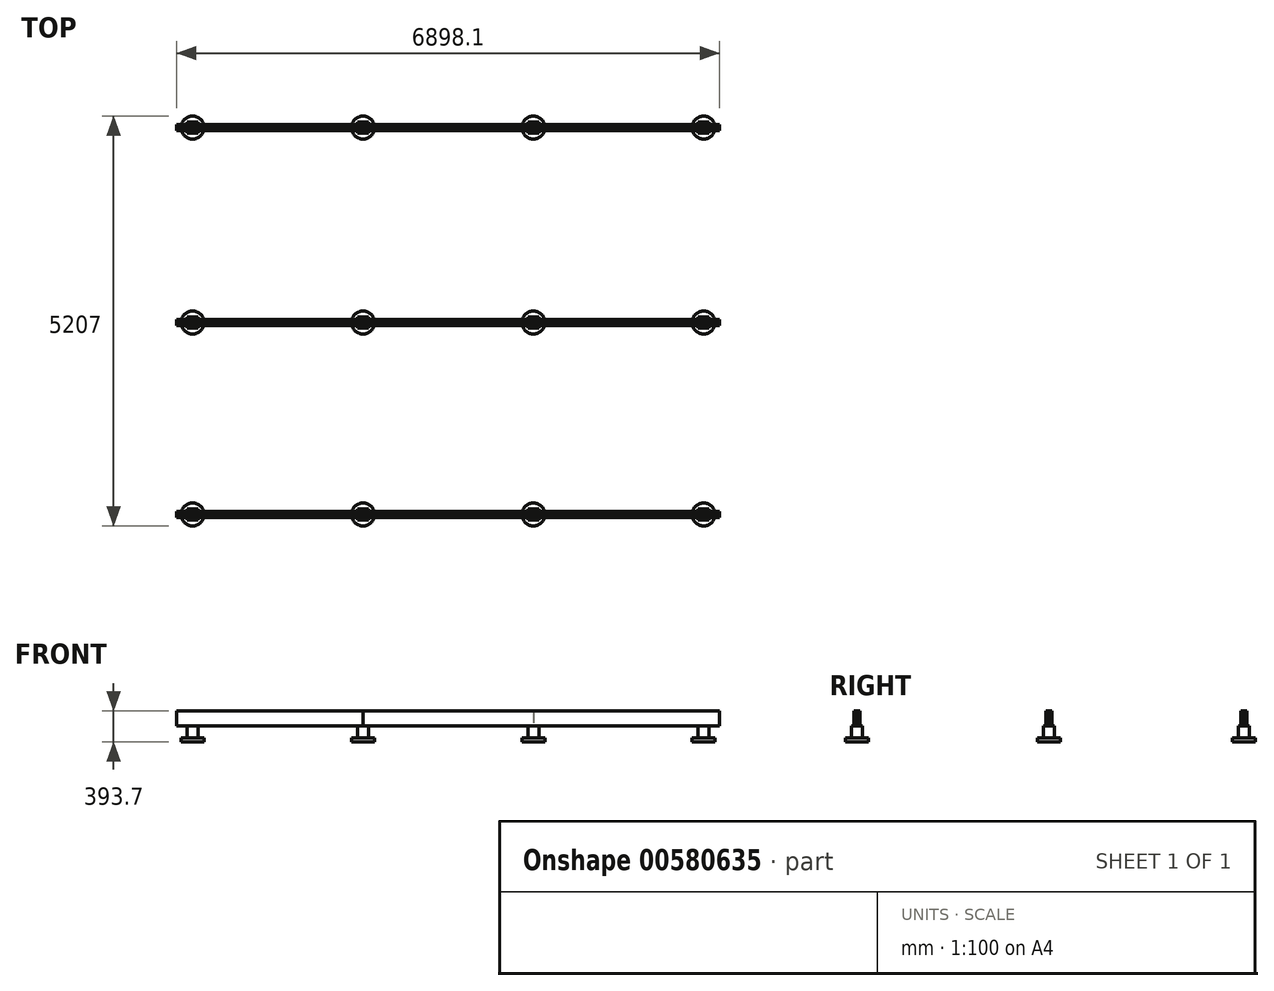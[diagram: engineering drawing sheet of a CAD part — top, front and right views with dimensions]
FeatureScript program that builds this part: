
annotation { "Feature Type Name" : "Feature", "Feature Type Description" : "" }
export const myFeature = defineFeature(function(context is Context, id is Id, definition is map)
    precondition{}
    {
        {
            var Q0;
            Q0=qCreatedBy(makeId("Top.planeOp"),FACE);
            var sketch = newSketch(context, id + "F0", { "sketchPlane" : qUnion([Q0])});
            skCircle(sketch, "E0", {"center": v(0, 0) * mm, "radius": 146.05 * mm});
            skCircle(sketch, "E1", {"center": v(2163.83, 0) * mm, "radius": 146.05 * mm});
            skCircle(sketch, "E2", {"center": v(4327.65, 0) * mm, "radius": 146.05 * mm});
            skCircle(sketch, "E3", {"center": v(6491.48, 0) * mm, "radius": 146.05 * mm});
            skCircle(sketch, "E4", {"center": v(0, -2476.5) * mm, "radius": 146.05 * mm});
            skCircle(sketch, "E5", {"center": v(2163.83, -2476.5) * mm, "radius": 146.05 * mm});
            skCircle(sketch, "E6", {"center": v(4327.65, -2476.5) * mm, "radius": 146.05 * mm});
            skCircle(sketch, "E7", {"center": v(6491.48, -2476.5) * mm, "radius": 146.05 * mm});
            skCircle(sketch, "E8", {"center": v(0, -4914.9) * mm, "radius": 146.05 * mm});
            skCircle(sketch, "E9", {"center": v(2163.83, -4914.9) * mm, "radius": 146.05 * mm});
            skCircle(sketch, "E10", {"center": v(4327.65, -4914.9) * mm, "radius": 146.05 * mm});
            skCircle(sketch, "E11", {"center": v(6491.48, -4914.9) * mm, "radius": 146.05 * mm});
            skSolve(sketch);
        }
        {
            var Q0;
            Q0=makeQuery(id+"F0.imprint","IMPRINT",FACE,{"disambiguationData":[TD([[makeQuery(id+"F0.imprint","IMPRINT",EDGE,{"derivedFrom":sQuery(id+"F0.wireOp",EDGE,"E3")}),1.0]])]});
            var Q1;
            Q1=makeQuery(id+"F0.imprint","IMPRINT",FACE,{"disambiguationData":[TD([[makeQuery(id+"F0.imprint","IMPRINT",EDGE,{"derivedFrom":sQuery(id+"F0.wireOp",EDGE,"E11")}),1.0]])]});
            var Q2;
            Q2=makeQuery(id+"F0.imprint","IMPRINT",FACE,{"disambiguationData":[TD([[makeQuery(id+"F0.imprint","IMPRINT",EDGE,{"derivedFrom":sQuery(id+"F0.wireOp",EDGE,"E5")}),1.0]])]});
            var Q3;
            Q3=makeQuery(id+"F0.imprint","IMPRINT",FACE,{"disambiguationData":[TD([[makeQuery(id+"F0.imprint","IMPRINT",EDGE,{"derivedFrom":sQuery(id+"F0.wireOp",EDGE,"E9")}),1.0]])]});
            var Q4;
            Q4=makeQuery(id+"F0.imprint","IMPRINT",FACE,{"disambiguationData":[TD([[makeQuery(id+"F0.imprint","IMPRINT",EDGE,{"derivedFrom":sQuery(id+"F0.wireOp",EDGE,"E4")}),1.0]])]});
            var Q5;
            Q5=makeQuery(id+"F0.imprint","IMPRINT",FACE,{"disambiguationData":[TD([[makeQuery(id+"F0.imprint","IMPRINT",EDGE,{"derivedFrom":sQuery(id+"F0.wireOp",EDGE,"E1")}),1.0]])]});
            var Q6;
            Q6=makeQuery(id+"F0.imprint","IMPRINT",FACE,{"disambiguationData":[TD([[makeQuery(id+"F0.imprint","IMPRINT",EDGE,{"derivedFrom":sQuery(id+"F0.wireOp",EDGE,"E10")}),1.0]])]});
            var Q7;
            Q7=makeQuery(id+"F0.imprint","IMPRINT",FACE,{"disambiguationData":[TD([[makeQuery(id+"F0.imprint","IMPRINT",EDGE,{"derivedFrom":sQuery(id+"F0.wireOp",EDGE,"E0")}),1.0]])]});
            var Q8;
            Q8=makeQuery(id+"F0.imprint","IMPRINT",FACE,{"disambiguationData":[TD([[makeQuery(id+"F0.imprint","IMPRINT",EDGE,{"derivedFrom":sQuery(id+"F0.wireOp",EDGE,"E2")}),1.0]])]});
            var Q9;
            Q9=makeQuery(id+"F0.imprint","IMPRINT",FACE,{"disambiguationData":[TD([[makeQuery(id+"F0.imprint","IMPRINT",EDGE,{"derivedFrom":sQuery(id+"F0.wireOp",EDGE,"E6")}),1.0]])]});
            var Q10;
            Q10=makeQuery(id+"F0.imprint","IMPRINT",FACE,{"disambiguationData":[TD([[makeQuery(id+"F0.imprint","IMPRINT",EDGE,{"derivedFrom":sQuery(id+"F0.wireOp",EDGE,"E7")}),1.0]])]});
            var Q11;
            Q11=makeQuery(id+"F0.imprint","IMPRINT",FACE,{"disambiguationData":[TD([[makeQuery(id+"F0.imprint","IMPRINT",EDGE,{"derivedFrom":sQuery(id+"F0.wireOp",EDGE,"E8")}),1.0]])]});
            extrude(context, id + "F1", {"entities" : qUnion([Q0, Q1, Q2, Q3, Q4, Q5, Q6, Q7, Q8, Q9, Q10, Q11]), "depth" : 50.8 * mm, "offsetDistance" : 25.4 * mm});
        }
        {
            var Q0;
            Q0=makeQuery(id+"F1.opExtrude","CAP_FACE",FACE,{"disambiguationData":[OSD([sQuery(id+"F0.wireOp",EDGE,"E0")])],"isStart":false});
            var sketch = newSketch(context, id + "F2", { "sketchPlane" : qUnion([Q0])});
            skLineSegment(sketch, "E12.bottom", {"start": v(69.85, -69.85) * mm, "end": v(-69.85, -69.85) * mm});
            skLineSegment(sketch, "E12.top", {"start": v(69.85, 69.85) * mm, "end": v(-69.85, 69.85) * mm});
            skLineSegment(sketch, "E12.left", {"start": v(69.85, -69.85) * mm, "end": v(69.85, 69.85) * mm});
            skLineSegment(sketch, "E12.right", {"start": v(-69.85, -69.85) * mm, "end": v(-69.85, 69.85) * mm});
            skPoint(sketch, "E12.middle", {"position": v(0, 0) * mm});
            skLineSegment(sketch, "E13.bottom", {"start": v(2233.68, -69.85) * mm, "end": v(2093.98, -69.85) * mm});
            skLineSegment(sketch, "E13.top", {"start": v(2233.68, 69.85) * mm, "end": v(2093.98, 69.85) * mm});
            skLineSegment(sketch, "E13.left", {"start": v(2233.68, -69.85) * mm, "end": v(2233.68, 69.85) * mm});
            skLineSegment(sketch, "E13.right", {"start": v(2093.98, -69.85) * mm, "end": v(2093.98, 69.85) * mm});
            skPoint(sketch, "E13.middle", {"position": v(2163.83, 0) * mm});
            skPoint(sketch, "E13.middle.positionSnap0", {"position": v(69.85, 0) * mm});
            skPoint(sketch, "E13.centerSnap0", {"position": v(69.85, 0) * mm});
            skLineSegment(sketch, "E14.bottom", {"start": v(4397.5, -69.85) * mm, "end": v(4257.8, -69.85) * mm});
            skLineSegment(sketch, "E14.top", {"start": v(4397.5, 69.85) * mm, "end": v(4257.8, 69.85) * mm});
            skLineSegment(sketch, "E14.left", {"start": v(4397.5, -69.85) * mm, "end": v(4397.5, 69.85) * mm});
            skLineSegment(sketch, "E14.right", {"start": v(4257.8, -69.85) * mm, "end": v(4257.8, 69.85) * mm});
            skPoint(sketch, "E14.middle", {"position": v(4327.65, 0) * mm});
            skLineSegment(sketch, "E15.bottom", {"start": v(6561.33, -69.85) * mm, "end": v(6421.63, -69.85) * mm});
            skLineSegment(sketch, "E15.top", {"start": v(6561.33, 69.85) * mm, "end": v(6421.63, 69.85) * mm});
            skLineSegment(sketch, "E15.left", {"start": v(6561.33, -69.85) * mm, "end": v(6561.33, 69.85) * mm});
            skLineSegment(sketch, "E15.right", {"start": v(6421.63, -69.85) * mm, "end": v(6421.63, 69.85) * mm});
            skPoint(sketch, "E15.middle", {"position": v(6491.48, 0) * mm});
            skLineSegment(sketch, "E16.bottom", {"start": v(69.85, -2546.35) * mm, "end": v(-69.85, -2546.35) * mm});
            skLineSegment(sketch, "E16.top", {"start": v(69.85, -2406.65) * mm, "end": v(-69.85, -2406.65) * mm});
            skLineSegment(sketch, "E16.left", {"start": v(69.85, -2546.35) * mm, "end": v(69.85, -2406.65) * mm});
            skLineSegment(sketch, "E16.right", {"start": v(-69.85, -2546.35) * mm, "end": v(-69.85, -2406.65) * mm});
            skPoint(sketch, "E16.middle", {"position": v(0, -2476.5) * mm});
            skLineSegment(sketch, "E17.bottom", {"start": v(2233.68, -2546.35) * mm, "end": v(2093.98, -2546.35) * mm});
            skLineSegment(sketch, "E17.top", {"start": v(2233.68, -2406.65) * mm, "end": v(2093.98, -2406.65) * mm});
            skLineSegment(sketch, "E17.left", {"start": v(2233.68, -2546.35) * mm, "end": v(2233.68, -2406.65) * mm});
            skLineSegment(sketch, "E17.right", {"start": v(2093.98, -2546.35) * mm, "end": v(2093.98, -2406.65) * mm});
            skPoint(sketch, "E17.middle", {"position": v(2163.83, -2476.5) * mm});
            skLineSegment(sketch, "E18.bottom", {"start": v(4397.5, -2546.35) * mm, "end": v(4257.8, -2546.35) * mm});
            skLineSegment(sketch, "E18.top", {"start": v(4397.5, -2406.65) * mm, "end": v(4257.8, -2406.65) * mm});
            skLineSegment(sketch, "E18.left", {"start": v(4397.5, -2546.35) * mm, "end": v(4397.5, -2406.65) * mm});
            skLineSegment(sketch, "E18.right", {"start": v(4257.8, -2546.35) * mm, "end": v(4257.8, -2406.65) * mm});
            skPoint(sketch, "E18.middle", {"position": v(4327.65, -2476.5) * mm});
            skLineSegment(sketch, "E19.bottom", {"start": v(6561.33, -2546.35) * mm, "end": v(6421.63, -2546.35) * mm});
            skLineSegment(sketch, "E19.top", {"start": v(6561.33, -2406.65) * mm, "end": v(6421.63, -2406.65) * mm});
            skLineSegment(sketch, "E19.left", {"start": v(6561.33, -2546.35) * mm, "end": v(6561.33, -2406.65) * mm});
            skLineSegment(sketch, "E19.right", {"start": v(6421.63, -2546.35) * mm, "end": v(6421.63, -2406.65) * mm});
            skPoint(sketch, "E19.middle", {"position": v(6491.48, -2476.5) * mm});
            skLineSegment(sketch, "E20.bottom", {"start": v(69.85, -4984.75) * mm, "end": v(-69.85, -4984.75) * mm});
            skLineSegment(sketch, "E20.top", {"start": v(69.85, -4845.05) * mm, "end": v(-69.85, -4845.05) * mm});
            skLineSegment(sketch, "E20.left", {"start": v(69.85, -4984.75) * mm, "end": v(69.85, -4845.05) * mm});
            skLineSegment(sketch, "E20.right", {"start": v(-69.85, -4984.75) * mm, "end": v(-69.85, -4845.05) * mm});
            skPoint(sketch, "E20.middle", {"position": v(0, -4914.9) * mm});
            skLineSegment(sketch, "E21.bottom", {"start": v(2233.68, -4984.75) * mm, "end": v(2093.98, -4984.75) * mm});
            skLineSegment(sketch, "E21.top", {"start": v(2233.68, -4845.05) * mm, "end": v(2093.98, -4845.05) * mm});
            skLineSegment(sketch, "E21.left", {"start": v(2233.68, -4984.75) * mm, "end": v(2233.68, -4845.05) * mm});
            skLineSegment(sketch, "E21.right", {"start": v(2093.98, -4984.75) * mm, "end": v(2093.98, -4845.05) * mm});
            skPoint(sketch, "E21.middle", {"position": v(2163.83, -4914.9) * mm});
            skLineSegment(sketch, "E22.bottom", {"start": v(4397.5, -4984.75) * mm, "end": v(4257.8, -4984.75) * mm});
            skLineSegment(sketch, "E22.top", {"start": v(4397.5, -4845.05) * mm, "end": v(4257.8, -4845.05) * mm});
            skLineSegment(sketch, "E22.left", {"start": v(4397.5, -4984.75) * mm, "end": v(4397.5, -4845.05) * mm});
            skLineSegment(sketch, "E22.right", {"start": v(4257.8, -4984.75) * mm, "end": v(4257.8, -4845.05) * mm});
            skPoint(sketch, "E22.middle", {"position": v(4327.65, -4914.9) * mm});
            skLineSegment(sketch, "E23.bottom", {"start": v(6561.33, -4984.75) * mm, "end": v(6421.63, -4984.75) * mm});
            skLineSegment(sketch, "E23.top", {"start": v(6561.33, -4845.05) * mm, "end": v(6421.63, -4845.05) * mm});
            skLineSegment(sketch, "E23.left", {"start": v(6561.33, -4984.75) * mm, "end": v(6561.33, -4845.05) * mm});
            skLineSegment(sketch, "E23.right", {"start": v(6421.63, -4984.75) * mm, "end": v(6421.63, -4845.05) * mm});
            skPoint(sketch, "E23.middle", {"position": v(6491.48, -4914.9) * mm});
            skSolve(sketch);
        }
        {
            var Q0;
            Q0 = qSketchRegion(id + "F2", true);
            extrude(context, id + "F3", {"entities" : qUnion([Q0]), "depth" : 152.4 * mm, "offsetDistance" : 25.4 * mm});
        }
        {
            var Q0;
            Q0=makeQuery(id+"F3.opExtrude","CAP_FACE",FACE,{"disambiguationData":[OSD([sQuery(id+"F2.wireOp",EDGE,"E12.bottom"),sQuery(id+"F2.wireOp",EDGE,"E12.top"),sQuery(id+"F2.wireOp",EDGE,"E12.left"),sQuery(id+"F2.wireOp",EDGE,"E12.right")])],"isStart":false});
            var sketch = newSketch(context, id + "F4", { "sketchPlane" : qUnion([Q0])});
            skLineSegment(sketch, "E24.bottom", {"start": v(2163.83, -38.1) * mm, "end": v(-203.2, -38.1) * mm});
            skLineSegment(sketch, "E24.top", {"start": v(2163.83, 0) * mm, "end": v(-203.2, 0) * mm});
            skLineSegment(sketch, "E24.left", {"start": v(2163.83, -38.1) * mm, "end": v(2163.83, 0) * mm});
            skLineSegment(sketch, "E24.right", {"start": v(-203.2, -38.1) * mm, "end": v(-203.2, 0) * mm});
            skPoint(sketch, "E24.middle", {"position": v(980.31, -19.05) * mm});
            skSolve(sketch);
        }
        {
            var Q0;
            Q0 = qSketchRegion(id + "F4", true);
            extrude(context, id + "F5", {"entities" : qUnion([Q0]), "depth" : 190.5 * mm, "offsetDistance" : 25.4 * mm});
        }
        {
            var Q0;
            Q0=makeQuery(id+"F3.opExtrude","CAP_FACE",FACE,{"disambiguationData":[OSD([sQuery(id+"F2.wireOp",EDGE,"E12.bottom"),sQuery(id+"F2.wireOp",EDGE,"E12.top"),sQuery(id+"F2.wireOp",EDGE,"E12.left"),sQuery(id+"F2.wireOp",EDGE,"E12.right")])],"isStart":false});
            var sketch = newSketch(context, id + "F6", { "sketchPlane" : qUnion([Q0])});
            skLineSegment(sketch, "E25.bottom", {"start": v(-203.2, 0) * mm, "end": v(4327.65, 0) * mm});
            skLineSegment(sketch, "E25.top", {"start": v(-203.2, 38.1) * mm, "end": v(4327.65, 38.1) * mm});
            skLineSegment(sketch, "E25.left", {"start": v(-203.2, 0) * mm, "end": v(-203.2, 38.1) * mm});
            skLineSegment(sketch, "E25.right", {"start": v(4327.65, 0) * mm, "end": v(4327.65, 38.1) * mm});
            skSolve(sketch);
        }
        {
            var Q0;
            {var subQ0=sQuery(id+"F6.wireOp",EDGE,"E25.right");Q0=makeQuery(id+"F6.imprint","IMPRINT",FACE,{"disambiguationData":[TD([[makeQuery(id+"F6.imprint","IMPRINT",EDGE,{"derivedFrom":subQ0}),1.0]])]});}
            var Q1;
            {var subQ0=sQuery(id+"F6.wireOp",EDGE,"E25.bottom");var subQ1=makeQuery(id+"F3.opExtrude","CAP_EDGE",EDGE,{"disambiguationData":[OSD([sQuery(id+"F2.wireOp",EDGE,"E12.right")])],"isStart":false});var subQ2=makeQuery(id+"F6.imprint","INTERSECT",VERTEX,{"derivedFrom":[subQ1,subQ0]});Q1=makeQuery(id+"F6.imprint","IMPRINT",FACE,{"disambiguationData":[TD([[makeQuery(id+"F6.imprint","IMPRINT",EDGE,{"disambiguationData":[TD([[subQ2,-1.0]])],"derivedFrom":subQ0}),1.0]])]});}
            var Q2;
            {var subQ0=sQuery(id+"F6.wireOp",EDGE,"E25.left");Q2=makeQuery(id+"F6.imprint","IMPRINT",FACE,{"disambiguationData":[TD([[makeQuery(id+"F6.imprint","IMPRINT",EDGE,{"derivedFrom":subQ0}),-1.0]])]});}
            extrude(context, id + "F7", {"entities" : qUnion([Q0, Q1, Q2]), "depth" : 190.5 * mm, "offsetDistance" : 25.4 * mm});
        }
        {
            var Q0;
            Q0=makeQuery(id+"F3.opExtrude","CAP_FACE",FACE,{"disambiguationData":[OSD([sQuery(id+"F2.wireOp",EDGE,"E16.bottom"),sQuery(id+"F2.wireOp",EDGE,"E16.top"),sQuery(id+"F2.wireOp",EDGE,"E16.left"),sQuery(id+"F2.wireOp",EDGE,"E16.right")])],"isStart":false});
            var sketch = newSketch(context, id + "F8", { "sketchPlane" : qUnion([Q0])});
            skLineSegment(sketch, "E26.bottom", {"start": v(-203.2, -2438.4) * mm, "end": v(4327.87, -2438.4) * mm});
            skLineSegment(sketch, "E26.top", {"start": v(-203.2, -2476.5) * mm, "end": v(4327.87, -2476.5) * mm});
            skLineSegment(sketch, "E26.left", {"start": v(-203.2, -2438.4) * mm, "end": v(-203.2, -2476.5) * mm});
            skLineSegment(sketch, "E26.right", {"start": v(4327.87, -2438.4) * mm, "end": v(4327.87, -2476.5) * mm});
            skSolve(sketch);
        }
        {
            var Q0;
            {var subQ0=sQuery(id+"F8.wireOp",EDGE,"E26.bottom");var subQ1=makeQuery(id+"F3.opExtrude","CAP_EDGE",EDGE,{"disambiguationData":[OSD([sQuery(id+"F2.wireOp",EDGE,"E16.right")])],"isStart":false});var subQ2=makeQuery(id+"F8.imprint","INTERSECT",VERTEX,{"derivedFrom":[subQ1,subQ0]});Q0=makeQuery(id+"F8.imprint","IMPRINT",FACE,{"disambiguationData":[TD([[makeQuery(id+"F8.imprint","IMPRINT",EDGE,{"disambiguationData":[TD([[subQ2,-1.0]])],"derivedFrom":subQ0}),-1.0]])]});}
            var Q1;
            {var subQ0=sQuery(id+"F8.wireOp",EDGE,"E26.left");Q1=makeQuery(id+"F8.imprint","IMPRINT",FACE,{"disambiguationData":[TD([[makeQuery(id+"F8.imprint","IMPRINT",EDGE,{"derivedFrom":subQ0}),1.0]])]});}
            var Q2;
            {var subQ0=sQuery(id+"F8.wireOp",EDGE,"E26.right");Q2=makeQuery(id+"F8.imprint","IMPRINT",FACE,{"disambiguationData":[TD([[makeQuery(id+"F8.imprint","IMPRINT",EDGE,{"derivedFrom":subQ0}),-1.0]])]});}
            extrude(context, id + "F9", {"entities" : qUnion([Q0, Q1, Q2]), "depth" : 190.5 * mm, "offsetDistance" : 25.4 * mm});
        }
        {
            var Q0;
            Q0=makeQuery(id+"F3.opExtrude","CAP_FACE",FACE,{"disambiguationData":[OSD([sQuery(id+"F2.wireOp",EDGE,"E14.bottom"),sQuery(id+"F2.wireOp",EDGE,"E14.top"),sQuery(id+"F2.wireOp",EDGE,"E14.left"),sQuery(id+"F2.wireOp",EDGE,"E14.right")])],"isStart":false});
            var sketch = newSketch(context, id + "F10", { "sketchPlane" : qUnion([Q0])});
            skLineSegment(sketch, "E27.bottom", {"start": v(4327.65, 38.1) * mm, "end": v(6694.68, 38.1) * mm});
            skLineSegment(sketch, "E27.top", {"start": v(4327.65, 0) * mm, "end": v(6694.68, 0) * mm});
            skLineSegment(sketch, "E27.left", {"start": v(4327.65, 38.1) * mm, "end": v(4327.65, 0) * mm});
            skLineSegment(sketch, "E27.right", {"start": v(6694.68, 38.1) * mm, "end": v(6694.68, 0) * mm});
            skSolve(sketch);
        }
        {
            var Q0;
            {var subQ0=sQuery(id+"F10.wireOp",EDGE,"E27.left");Q0=makeQuery(id+"F10.imprint","IMPRINT",FACE,{"disambiguationData":[TD([[makeQuery(id+"F10.imprint","IMPRINT",EDGE,{"derivedFrom":subQ0}),1.0]])]});}
            var Q1;
            {var subQ0=sQuery(id+"F10.wireOp",EDGE,"E27.right");Q1=makeQuery(id+"F10.imprint","IMPRINT",FACE,{"disambiguationData":[TD([[makeQuery(id+"F10.imprint","IMPRINT",EDGE,{"derivedFrom":subQ0}),-1.0]])]});}
            extrude(context, id + "F11", {"entities" : qUnion([Q0, Q1]), "depth" : 190.5 * mm, "offsetDistance" : 25.4 * mm});
        }
        {
            var Q0;
            Q0=makeQuery(id+"F3.opExtrude","CAP_FACE",FACE,{"disambiguationData":[OSD([sQuery(id+"F2.wireOp",EDGE,"E13.bottom"),sQuery(id+"F2.wireOp",EDGE,"E13.top"),sQuery(id+"F2.wireOp",EDGE,"E13.left"),sQuery(id+"F2.wireOp",EDGE,"E13.right")])],"isStart":false});
            var sketch = newSketch(context, id + "F12", { "sketchPlane" : qUnion([Q0])});
            skLineSegment(sketch, "E28.bottom", {"start": v(2163.83, 0) * mm, "end": v(6694.9, 0) * mm});
            skLineSegment(sketch, "E28.top", {"start": v(2163.83, -38.1) * mm, "end": v(6694.9, -38.1) * mm});
            skLineSegment(sketch, "E28.left", {"start": v(2163.83, 0) * mm, "end": v(2163.83, -38.1) * mm});
            skLineSegment(sketch, "E28.right", {"start": v(6694.9, 0) * mm, "end": v(6694.9, -38.1) * mm});
            skSolve(sketch);
        }
        {
            var Q0;
            {var subQ0=sQuery(id+"F12.wireOp",EDGE,"E28.left");Q0=makeQuery(id+"F12.imprint","IMPRINT",FACE,{"disambiguationData":[TD([[makeQuery(id+"F12.imprint","IMPRINT",EDGE,{"derivedFrom":subQ0}),1.0]])]});}
            var Q1;
            {var subQ0=sQuery(id+"F12.wireOp",EDGE,"E28.right");Q1=makeQuery(id+"F12.imprint","IMPRINT",FACE,{"disambiguationData":[TD([[makeQuery(id+"F12.imprint","IMPRINT",EDGE,{"derivedFrom":subQ0}),-1.0]])]});}
            extrude(context, id + "F13", {"entities" : qUnion([Q0, Q1]), "depth" : 190.5 * mm, "offsetDistance" : 25.4 * mm});
        }
        {
            var Q0;
            Q0=makeQuery(id+"F3.opExtrude","CAP_FACE",FACE,{"disambiguationData":[OSD([sQuery(id+"F2.wireOp",EDGE,"E20.bottom"),sQuery(id+"F2.wireOp",EDGE,"E20.top"),sQuery(id+"F2.wireOp",EDGE,"E20.left"),sQuery(id+"F2.wireOp",EDGE,"E20.right")])],"isStart":false});
            var sketch = newSketch(context, id + "F14", { "sketchPlane" : qUnion([Q0])});
            skLineSegment(sketch, "E29.bottom", {"start": v(-203.2, -4876.8) * mm, "end": v(4327.87, -4876.8) * mm});
            skLineSegment(sketch, "E29.top", {"start": v(-203.2, -4914.9) * mm, "end": v(4327.87, -4914.9) * mm});
            skLineSegment(sketch, "E29.left", {"start": v(-203.2, -4876.8) * mm, "end": v(-203.2, -4914.9) * mm});
            skLineSegment(sketch, "E29.right", {"start": v(4327.87, -4876.8) * mm, "end": v(4327.87, -4914.9) * mm});
            skSolve(sketch);
        }
        {
            var Q0;
            {var subQ0=sQuery(id+"F14.wireOp",EDGE,"E29.left");Q0=makeQuery(id+"F14.imprint","IMPRINT",FACE,{"disambiguationData":[TD([[makeQuery(id+"F14.imprint","IMPRINT",EDGE,{"derivedFrom":subQ0}),1.0]])]});}
            var Q1;
            {var subQ0=sQuery(id+"F14.wireOp",EDGE,"E29.bottom");var subQ1=makeQuery(id+"F3.opExtrude","CAP_EDGE",EDGE,{"disambiguationData":[OSD([sQuery(id+"F2.wireOp",EDGE,"E20.right")])],"isStart":false});var subQ2=makeQuery(id+"F14.imprint","INTERSECT",VERTEX,{"derivedFrom":[subQ1,subQ0]});Q1=makeQuery(id+"F14.imprint","IMPRINT",FACE,{"disambiguationData":[TD([[makeQuery(id+"F14.imprint","IMPRINT",EDGE,{"disambiguationData":[TD([[subQ2,-1.0]])],"derivedFrom":subQ0}),-1.0]])]});}
            var Q2;
            {var subQ0=sQuery(id+"F14.wireOp",EDGE,"E29.right");Q2=makeQuery(id+"F14.imprint","IMPRINT",FACE,{"disambiguationData":[TD([[makeQuery(id+"F14.imprint","IMPRINT",EDGE,{"derivedFrom":subQ0}),-1.0]])]});}
            extrude(context, id + "F15", {"entities" : qUnion([Q0, Q1, Q2]), "depth" : 190.5 * mm, "offsetDistance" : 25.4 * mm});
        }
        {
            var Q0;
            Q0=makeQuery(id+"F3.opExtrude","CAP_FACE",FACE,{"disambiguationData":[OSD([sQuery(id+"F2.wireOp",EDGE,"E16.bottom"),sQuery(id+"F2.wireOp",EDGE,"E16.top"),sQuery(id+"F2.wireOp",EDGE,"E16.left"),sQuery(id+"F2.wireOp",EDGE,"E16.right")])],"isStart":false});
            var sketch = newSketch(context, id + "F16", { "sketchPlane" : qUnion([Q0])});
            skLineSegment(sketch, "E30.bottom", {"start": v(-203.2, -2476.5) * mm, "end": v(2163.83, -2476.5) * mm});
            skLineSegment(sketch, "E30.top", {"start": v(-203.2, -2514.6) * mm, "end": v(2163.83, -2514.6) * mm});
            skLineSegment(sketch, "E30.left", {"start": v(-203.2, -2476.5) * mm, "end": v(-203.2, -2514.6) * mm});
            skLineSegment(sketch, "E30.right", {"start": v(2163.83, -2476.5) * mm, "end": v(2163.83, -2514.6) * mm});
            skSolve(sketch);
        }
        {
            var Q0;
            {var subQ0=sQuery(id+"F16.wireOp",EDGE,"E30.left");Q0=makeQuery(id+"F16.imprint","IMPRINT",FACE,{"disambiguationData":[TD([[makeQuery(id+"F16.imprint","IMPRINT",EDGE,{"derivedFrom":subQ0}),1.0]])]});}
            var Q1;
            {var subQ0=sQuery(id+"F16.wireOp",EDGE,"E30.bottom");var subQ1=makeQuery(id+"F3.opExtrude","CAP_EDGE",EDGE,{"disambiguationData":[OSD([sQuery(id+"F2.wireOp",EDGE,"E16.right")])],"isStart":false});var subQ2=makeQuery(id+"F16.imprint","INTERSECT",VERTEX,{"derivedFrom":[subQ1,subQ0]});Q1=makeQuery(id+"F16.imprint","IMPRINT",FACE,{"disambiguationData":[TD([[makeQuery(id+"F16.imprint","IMPRINT",EDGE,{"disambiguationData":[TD([[subQ2,-1.0]])],"derivedFrom":subQ0}),-1.0]])]});}
            var Q2;
            {var subQ0=sQuery(id+"F16.wireOp",EDGE,"E30.right");Q2=makeQuery(id+"F16.imprint","IMPRINT",FACE,{"disambiguationData":[TD([[makeQuery(id+"F16.imprint","IMPRINT",EDGE,{"derivedFrom":subQ0}),-1.0]])]});}
            extrude(context, id + "F17", {"entities" : qUnion([Q0, Q1, Q2]), "depth" : 190.5 * mm, "offsetDistance" : 25.4 * mm});
        }
        {
            var Q0;
            Q0=makeQuery(id+"F3.opExtrude","CAP_FACE",FACE,{"disambiguationData":[OSD([sQuery(id+"F2.wireOp",EDGE,"E20.bottom"),sQuery(id+"F2.wireOp",EDGE,"E20.top"),sQuery(id+"F2.wireOp",EDGE,"E20.left"),sQuery(id+"F2.wireOp",EDGE,"E20.right")])],"isStart":false});
            var sketch = newSketch(context, id + "F18", { "sketchPlane" : qUnion([Q0])});
            skLineSegment(sketch, "E31.bottom", {"start": v(-203.2, -4914.9) * mm, "end": v(2163.83, -4914.9) * mm});
            skLineSegment(sketch, "E31.top", {"start": v(-203.2, -4953) * mm, "end": v(2163.83, -4953) * mm});
            skLineSegment(sketch, "E31.left", {"start": v(-203.2, -4914.9) * mm, "end": v(-203.2, -4953) * mm});
            skLineSegment(sketch, "E31.right", {"start": v(2163.83, -4914.9) * mm, "end": v(2163.83, -4953) * mm});
            skSolve(sketch);
        }
        {
            var Q0;
            {var subQ0=sQuery(id+"F18.wireOp",EDGE,"E31.left");Q0=makeQuery(id+"F18.imprint","IMPRINT",FACE,{"disambiguationData":[TD([[makeQuery(id+"F18.imprint","IMPRINT",EDGE,{"derivedFrom":subQ0}),1.0]])]});}
            var Q1;
            {var subQ0=sQuery(id+"F18.wireOp",EDGE,"E31.bottom");var subQ1=makeQuery(id+"F3.opExtrude","CAP_EDGE",EDGE,{"disambiguationData":[OSD([sQuery(id+"F2.wireOp",EDGE,"E20.right")])],"isStart":false});var subQ2=makeQuery(id+"F18.imprint","INTERSECT",VERTEX,{"derivedFrom":[subQ1,subQ0]});Q1=makeQuery(id+"F18.imprint","IMPRINT",FACE,{"disambiguationData":[TD([[makeQuery(id+"F18.imprint","IMPRINT",EDGE,{"disambiguationData":[TD([[subQ2,-1.0]])],"derivedFrom":subQ0}),-1.0]])]});}
            var Q2;
            {var subQ0=sQuery(id+"F18.wireOp",EDGE,"E31.right");Q2=makeQuery(id+"F18.imprint","IMPRINT",FACE,{"disambiguationData":[TD([[makeQuery(id+"F18.imprint","IMPRINT",EDGE,{"derivedFrom":subQ0}),-1.0]])]});}
            extrude(context, id + "F19", {"entities" : qUnion([Q0, Q1, Q2]), "depth" : 190.5 * mm, "offsetDistance" : 25.4 * mm});
        }
        {
            var Q0;
            Q0=makeQuery(id+"F3.opExtrude","CAP_FACE",FACE,{"disambiguationData":[OSD([sQuery(id+"F2.wireOp",EDGE,"E17.bottom"),sQuery(id+"F2.wireOp",EDGE,"E17.top"),sQuery(id+"F2.wireOp",EDGE,"E17.left"),sQuery(id+"F2.wireOp",EDGE,"E17.right")])],"isStart":false});
            var sketch = newSketch(context, id + "F20", { "sketchPlane" : qUnion([Q0])});
            skLineSegment(sketch, "E32.bottom", {"start": v(2163.83, -2476.5) * mm, "end": v(6694.9, -2476.5) * mm});
            skLineSegment(sketch, "E32.top", {"start": v(2163.83, -2514.6) * mm, "end": v(6694.9, -2514.6) * mm});
            skLineSegment(sketch, "E32.left", {"start": v(2163.83, -2476.5) * mm, "end": v(2163.83, -2514.6) * mm});
            skLineSegment(sketch, "E32.right", {"start": v(6694.9, -2476.5) * mm, "end": v(6694.9, -2514.6) * mm});
            skSolve(sketch);
        }
        {
            var Q0;
            {var subQ0=sQuery(id+"F20.wireOp",EDGE,"E32.left");Q0=makeQuery(id+"F20.imprint","IMPRINT",FACE,{"disambiguationData":[TD([[makeQuery(id+"F20.imprint","IMPRINT",EDGE,{"derivedFrom":subQ0}),1.0]])]});}
            var Q1;
            {var subQ0=sQuery(id+"F20.wireOp",EDGE,"E32.right");Q1=makeQuery(id+"F20.imprint","IMPRINT",FACE,{"disambiguationData":[TD([[makeQuery(id+"F20.imprint","IMPRINT",EDGE,{"derivedFrom":subQ0}),-1.0]])]});}
            extrude(context, id + "F21", {"entities" : qUnion([Q0, Q1]), "depth" : 190.5 * mm, "offsetDistance" : 25.4 * mm});
        }
        {
            var Q0;
            Q0=makeQuery(id+"F3.opExtrude","CAP_FACE",FACE,{"disambiguationData":[OSD([sQuery(id+"F2.wireOp",EDGE,"E21.bottom"),sQuery(id+"F2.wireOp",EDGE,"E21.top"),sQuery(id+"F2.wireOp",EDGE,"E21.left"),sQuery(id+"F2.wireOp",EDGE,"E21.right")])],"isStart":false});
            var sketch = newSketch(context, id + "F22", { "sketchPlane" : qUnion([Q0])});
            skLineSegment(sketch, "E33.bottom", {"start": v(2163.83, -4914.9) * mm, "end": v(6694.9, -4914.9) * mm});
            skLineSegment(sketch, "E33.top", {"start": v(2163.83, -4953) * mm, "end": v(6694.9, -4953) * mm});
            skLineSegment(sketch, "E33.left", {"start": v(2163.83, -4914.9) * mm, "end": v(2163.83, -4953) * mm});
            skLineSegment(sketch, "E33.right", {"start": v(6694.9, -4914.9) * mm, "end": v(6694.9, -4953) * mm});
            skSolve(sketch);
        }
        {
            var Q0;
            {var subQ0=sQuery(id+"F22.wireOp",EDGE,"E33.right");Q0=makeQuery(id+"F22.imprint","IMPRINT",FACE,{"disambiguationData":[TD([[makeQuery(id+"F22.imprint","IMPRINT",EDGE,{"derivedFrom":subQ0}),-1.0]])]});}
            var Q1;
            {var subQ0=sQuery(id+"F22.wireOp",EDGE,"E33.left");Q1=makeQuery(id+"F22.imprint","IMPRINT",FACE,{"disambiguationData":[TD([[makeQuery(id+"F22.imprint","IMPRINT",EDGE,{"derivedFrom":subQ0}),1.0]])]});}
            extrude(context, id + "F23", {"entities" : qUnion([Q0, Q1]), "depth" : 190.5 * mm, "offsetDistance" : 25.4 * mm});
        }
        {
            var Q0;
            Q0=makeQuery(id+"F3.opExtrude","CAP_FACE",FACE,{"disambiguationData":[OSD([sQuery(id+"F2.wireOp",EDGE,"E18.bottom"),sQuery(id+"F2.wireOp",EDGE,"E18.top"),sQuery(id+"F2.wireOp",EDGE,"E18.left"),sQuery(id+"F2.wireOp",EDGE,"E18.right")])],"isStart":false});
            var sketch = newSketch(context, id + "F24", { "sketchPlane" : qUnion([Q0])});
            skLineSegment(sketch, "E34.bottom", {"start": v(4327.87, -2476.5) * mm, "end": v(6694.9, -2476.5) * mm});
            skLineSegment(sketch, "E34.top", {"start": v(4327.87, -2438.4) * mm, "end": v(6694.9, -2438.4) * mm});
            skLineSegment(sketch, "E34.left", {"start": v(4327.87, -2476.5) * mm, "end": v(4327.87, -2438.4) * mm});
            skLineSegment(sketch, "E34.right", {"start": v(6694.9, -2476.5) * mm, "end": v(6694.9, -2438.4) * mm});
            skSolve(sketch);
        }
        {
            var Q0;
            {var subQ0=sQuery(id+"F24.wireOp",EDGE,"E34.right");Q0=makeQuery(id+"F24.imprint","IMPRINT",FACE,{"disambiguationData":[TD([[makeQuery(id+"F24.imprint","IMPRINT",EDGE,{"derivedFrom":subQ0}),1.0]])]});}
            var Q1;
            {var subQ0=sQuery(id+"F24.wireOp",EDGE,"E34.left");Q1=makeQuery(id+"F24.imprint","IMPRINT",FACE,{"disambiguationData":[TD([[makeQuery(id+"F24.imprint","IMPRINT",EDGE,{"derivedFrom":subQ0}),-1.0]])]});}
            extrude(context, id + "F25", {"entities" : qUnion([Q0, Q1]), "depth" : 190.5 * mm, "offsetDistance" : 25.4 * mm});
        }
        {
            var Q0;
            Q0=makeQuery(id+"F3.opExtrude","CAP_FACE",FACE,{"disambiguationData":[OSD([sQuery(id+"F2.wireOp",EDGE,"E22.bottom"),sQuery(id+"F2.wireOp",EDGE,"E22.top"),sQuery(id+"F2.wireOp",EDGE,"E22.left"),sQuery(id+"F2.wireOp",EDGE,"E22.right")])],"isStart":false});
            var sketch = newSketch(context, id + "F26", { "sketchPlane" : qUnion([Q0])});
            skLineSegment(sketch, "E35.bottom", {"start": v(4327.87, -4914.9) * mm, "end": v(6694.9, -4914.9) * mm});
            skLineSegment(sketch, "E35.top", {"start": v(4327.87, -4876.8) * mm, "end": v(6694.9, -4876.8) * mm});
            skLineSegment(sketch, "E35.left", {"start": v(4327.87, -4914.9) * mm, "end": v(4327.87, -4876.8) * mm});
            skLineSegment(sketch, "E35.right", {"start": v(6694.9, -4914.9) * mm, "end": v(6694.9, -4876.8) * mm});
            skSolve(sketch);
        }
        {
            var Q0;
            {var subQ0=sQuery(id+"F26.wireOp",EDGE,"E35.right");Q0=makeQuery(id+"F26.imprint","IMPRINT",FACE,{"disambiguationData":[TD([[makeQuery(id+"F26.imprint","IMPRINT",EDGE,{"derivedFrom":subQ0}),1.0]])]});}
            var Q1;
            {var subQ0=sQuery(id+"F26.wireOp",EDGE,"E35.left");Q1=makeQuery(id+"F26.imprint","IMPRINT",FACE,{"disambiguationData":[TD([[makeQuery(id+"F26.imprint","IMPRINT",EDGE,{"derivedFrom":subQ0}),-1.0]])]});}
            extrude(context, id + "F27", {"entities" : qUnion([Q0, Q1]), "depth" : 190.5 * mm, "offsetDistance" : 25.4 * mm});
        }
    });
